# Revit family: QF_Vollrath_74701D
name_source: partatom
category: Specialty Equipment
revit_build: Autodesk Revit 2016 (Build: 20151007_0715(x64)
units: mm (PartAtom-declared; Revit-internal decimal feet)

## family parameters
Always vertical = Yes
Cut with Voids When Loaded = No
OmniClass Number = 23.40.40.14.17.31
OmniClass Title = Small Specialized Cooking Equipment
Part Type = Normal
Room Calculation Point = No
Round Connector Dimension = Use Diameter
Shared = No
Work Plane-Based = Yes

## types (1)
- QF_Vollrath_74701D
    Apparent Power = 804 VA
    Assembly Code = E1090320
    CSI MasterFormat = 11 44 00
    Conn Plug = NEMA 5-15P
    Cycle = 60 Hz
    Default Elevation = 4' - 0"
    Description = 7 qt. Induction Rethermalizer, Drop-In
    Elec Conn Connection Height = -0' - 9 1/4"
    FL Amps = 7 A
    Foodservice Equipment Identifier = Yes
    Manufacturer = Vollrath
    Material = QF_Finishes_Black
    Model = 74701D
    Outer Diameter = 0' - 11 7/8"
    Phase = 1
    URL = www.vollrathco.com
    Volts = 120 V
    Watts = 800 W
    Weight in Pounds = 12.4

## geometry (parser evidence)
native form markers: Blend x45, Sweep x2
no freeform markers — native parametric forms only
